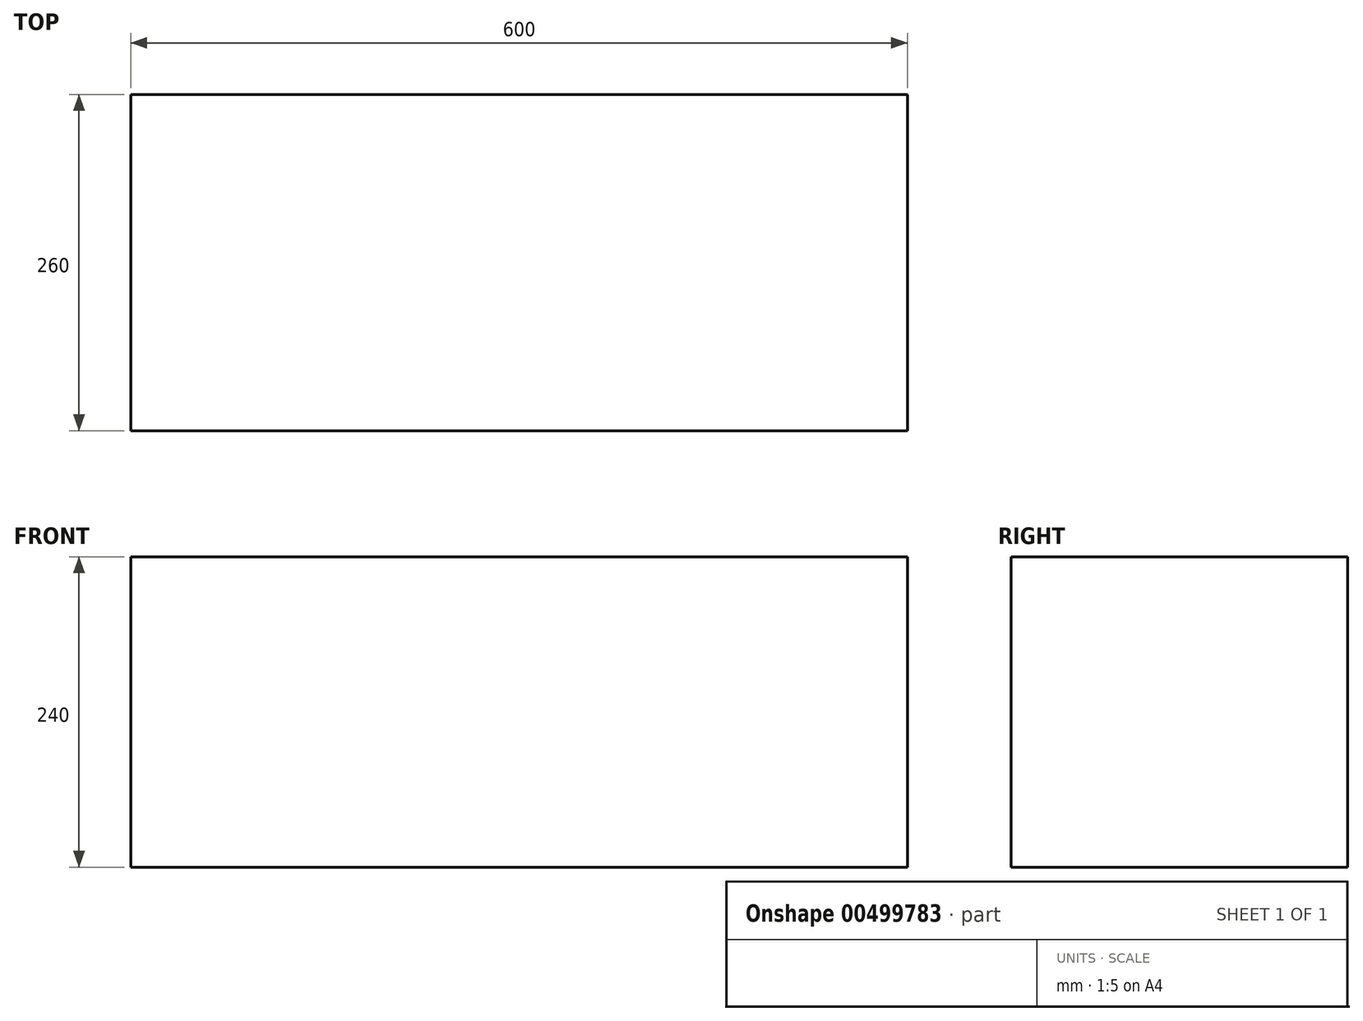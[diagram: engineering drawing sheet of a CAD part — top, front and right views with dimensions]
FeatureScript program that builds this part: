
annotation { "Feature Type Name" : "Feature", "Feature Type Description" : "" }
export const myFeature = defineFeature(function(context is Context, id is Id, definition is map)
    precondition{}
    {
        {
            var Q0;
            Q0=qCreatedBy(makeId("Front.planeOp"),FACE);
            var sketch = newSketch(context, id + "F0", { "sketchPlane" : qUnion([Q0])});
            skLineSegment(sketch, "E0.bottom", {"start": v(-313.67, -52.03) * mm, "end": v(286.33, -52.03) * mm});
            skLineSegment(sketch, "E0.top", {"start": v(-313.67, -292.03) * mm, "end": v(286.33, -292.03) * mm});
            skLineSegment(sketch, "E0.left", {"start": v(-313.67, -52.03) * mm, "end": v(-313.67, -292.03) * mm});
            skLineSegment(sketch, "E0.right", {"start": v(286.33, -52.03) * mm, "end": v(286.33, -292.03) * mm});
            skSolve(sketch);
        }
        {
            var Q0;
            Q0 = qSketchRegion(id + "F0", true);
            extrude(context, id + "F1", {"entities" : qUnion([Q0]), "depth" : 260 * mm});
        }
    });
